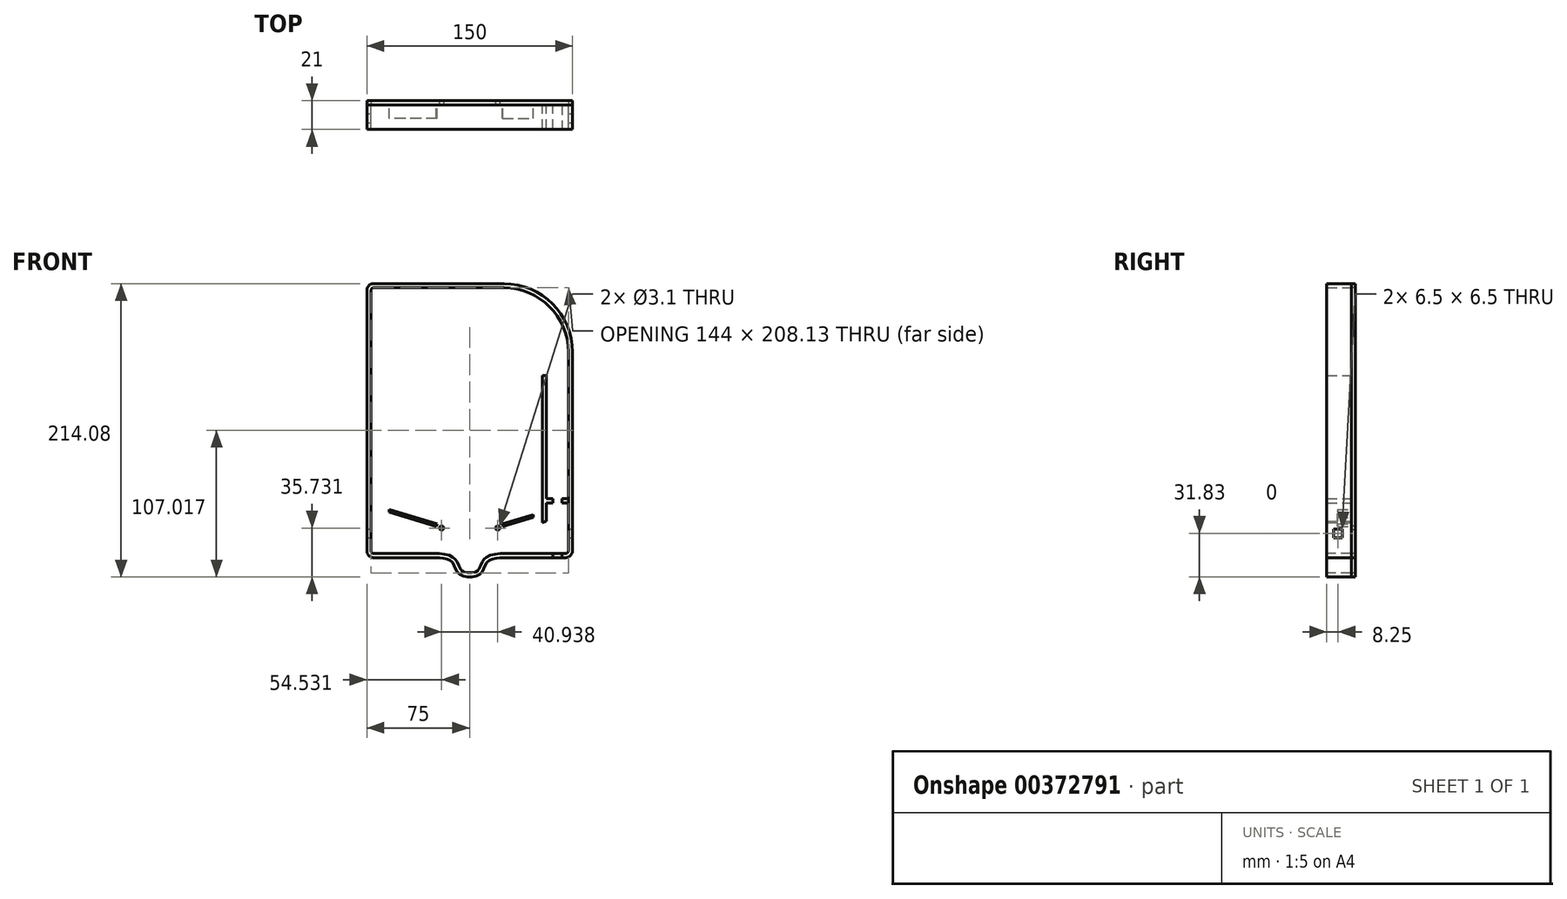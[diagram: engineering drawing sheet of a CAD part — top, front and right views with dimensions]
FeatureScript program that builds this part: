
annotation { "Feature Type Name" : "Feature", "Feature Type Description" : "" }
export const myFeature = defineFeature(function(context is Context, id is Id, definition is map)
    precondition{}
    {
        {
            var Q0;
            Q0=qCreatedBy(makeId("Front.planeOp"),FACE);
            var sketch = newSketch(context, id + "F0", { "sketchPlane" : qUnion([Q0])});
            skLineSegment(sketch, "E0.bottom", {"start": v(-70, 100) * mm, "end": v(25, 100) * mm});
            skLineSegment(sketch, "E0.top", {"start": v(-70, -100) * mm, "end": v(-25, -100) * mm});
            skLineSegment(sketch, "E0.left", {"start": v(-75, 95) * mm, "end": v(-75, -95) * mm});
            skLineSegment(sketch, "E0.right", {"start": v(75, 50) * mm, "end": v(75, -95) * mm});
            skPoint(sketch, "E1.visualSharp", {"position": v(75, 100) * mm});
            skArc(sketch, "E1.filletArc", {"start": v(75, 50) * mm, "mid": v(60.36, 85.36) * mm, "end": v(25, 100) * mm});
            skFitSpline(sketch, "E2", {"points": [v(-25, -100) * mm, v(-13, -103) * mm, v(-7.5, -112) * mm, v(7.5, -112) * mm, v(13, -103) * mm, v(25, -100) * mm], "startDerivative": vector(64.4, 0) * mm, "endDerivative": vector(59.8, 0) * mm});
            skLineSegment(sketch, "E3.trimOffspring", {"start": v(25, -100) * mm, "end": v(70, -100) * mm});
            skPoint(sketch, "E4.visualSharp", {"position": v(-75, -100) * mm});
            skArc(sketch, "E4.filletArc", {"start": v(-75, -95) * mm, "mid": v(-73.54, -98.54) * mm, "end": v(-70, -100) * mm});
            skPoint(sketch, "E5.visualSharp", {"position": v(75, -100) * mm});
            skArc(sketch, "E5.filletArc", {"start": v(70, -100) * mm, "mid": v(73.54, -98.54) * mm, "end": v(75, -95) * mm});
            skPoint(sketch, "E6.visualSharp", {"position": v(-75, 100) * mm});
            skArc(sketch, "E6.filletArc", {"start": v(-70, 100) * mm, "mid": v(-73.54, 98.54) * mm, "end": v(-75, 95) * mm});
            skArc(sketch, "E7.0", {"start": v(72, 50) * mm, "mid": v(58.23, 83.23) * mm, "end": v(25, 97) * mm});
            skLineSegment(sketch, "E7.1", {"start": v(-70, 97) * mm, "end": v(25, 97) * mm});
            skLineSegment(sketch, "E7.2", {"start": v(25, -97) * mm, "end": v(70, -97) * mm});
            skFitSpline(sketch, "E7.3", {"points": [v(-25, -97) * mm, v(-24.3, -97) * mm, v(-22.85, -97.02) * mm, v(-20.58, -97.16) * mm, v(-18.27, -97.45) * mm, v(-15.99, -97.96) * mm, v(-14.14, -98.64) * mm, v(-12.72, -99.4) * mm, v(-11.88, -99.98) * mm, v(-11.24, -100.52) * mm, v(-10.79, -100.96) * mm, v(-10.37, -101.43) * mm, v(-9.87, -102.07) * mm, v(-9.35, -102.88) * mm, v(-8.68, -104.15) * mm, v(-8.04, -105.65) * mm, v(-7.4, -107.23) * mm, v(-6.85, -108.28) * mm, v(-6.39, -108.93) * mm, v(-6.09, -109.26) * mm, v(-5.83, -109.5) * mm, v(-5.63, -109.66) * mm, v(-5.4, -109.82) * mm, v(-5.03, -110.03) * mm, v(-4.5, -110.3) * mm, v(-3.74, -110.57) * mm, v(-2.88, -110.79) * mm, v(-1.65, -111.01) * mm, v(0.01, -111.13) * mm, v(1.67, -111.01) * mm, v(2.9, -110.8) * mm, v(3.75, -110.57) * mm, v(4.5, -110.3) * mm, v(5.04, -110.04) * mm, v(5.4, -109.82) * mm, v(5.62, -109.66) * mm, v(5.82, -109.5) * mm, v(6.07, -109.27) * mm, v(6.36, -108.94) * mm, v(6.81, -108.3) * mm, v(7.35, -107.25) * mm, v(8, -105.66) * mm, v(8.65, -104.14) * mm, v(9.34, -102.85) * mm, v(9.88, -102.04) * mm, v(10.39, -101.4) * mm, v(10.82, -100.93) * mm, v(11.29, -100.48) * mm, v(11.94, -99.95) * mm, v(12.8, -99.37) * mm, v(14.25, -98.62) * mm, v(16.12, -97.95) * mm, v(18.43, -97.45) * mm, v(20.73, -97.16) * mm, v(22.96, -97.02) * mm, v(24.35, -97) * mm, v(25, -97) * mm]});
            skLineSegment(sketch, "E7.4", {"start": v(-70, -97) * mm, "end": v(-25, -97) * mm});
            skLineSegment(sketch, "E7.5", {"start": v(72, 50) * mm, "end": v(72, -95) * mm});
            skLineSegment(sketch, "E7.6", {"start": v(-72, 95) * mm, "end": v(-72, -95) * mm});
            skPoint(sketch, "E8.visualSharp", {"position": v(-72, -97) * mm});
            skArc(sketch, "E8.filletArc", {"start": v(-72, -95) * mm, "mid": v(-71.41, -96.41) * mm, "end": v(-70, -97) * mm});
            skPoint(sketch, "E9.visualSharp", {"position": v(72, -97) * mm});
            skArc(sketch, "E9.filletArc", {"start": v(70, -97) * mm, "mid": v(71.41, -96.41) * mm, "end": v(72, -95) * mm});
            skPoint(sketch, "E10.visualSharp", {"position": v(-72, 97) * mm});
            skArc(sketch, "E10.filletArc", {"start": v(-70, 97) * mm, "mid": v(-71.41, 96.41) * mm, "end": v(-72, 95) * mm});
            skSolve(sketch);
        }
        {
            var Q0;
            Q0=makeQuery(id+"F0.imprint","IMPRINT",FACE,{"disambiguationData":[TD([[makeQuery(id+"F0.imprint","IMPRINT",EDGE,{"derivedFrom":sQuery(id+"F0.wireOp",EDGE,"E0.bottom")}),-1.0]])]});
            extrude(context, id + "F1", {"entities" : qUnion([Q0]), "oppositeDirection" : true, "depth" : 3 * mm});
        }
        {
            var Q0;
            Q0=qCreatedBy(makeId("Front.planeOp"),FACE);
            var sketch = newSketch(context, id + "F2", { "sketchPlane" : qUnion([Q0])});
            skPoint(sketch, "E11.visualSharp", {"position": v(75, 100) * mm});
            skPoint(sketch, "E12.visualSharp", {"position": v(-75, -100) * mm});
            skPoint(sketch, "E13.visualSharp", {"position": v(75, -100) * mm});
            skPoint(sketch, "E14.visualSharp", {"position": v(-75, 100) * mm});
            skPoint(sketch, "E15.visualSharp", {"position": v(-72, -97) * mm});
            skPoint(sketch, "E16.visualSharp", {"position": v(72, -97.03) * mm});
            skPoint(sketch, "E17.visualSharp", {"position": v(-72, 97) * mm});
            skLineSegment(sketch, "E18", {"start": v(56, -76.55) * mm, "end": v(56, -60.03) * mm});
            skLineSegment(sketch, "E19.0", {"start": v(53, -74.41) * mm, "end": v(53, 32.97) * mm});
            skLineSegment(sketch, "E20", {"start": v(53, 32.97) * mm, "end": v(56, 32.97) * mm});
            skLineSegment(sketch, "E21", {"start": v(-23.73, -75.29) * mm, "end": v(-58.84, -64.8) * mm});
            skFitSpline(sketch, "E22", {"points": [v(-72, -68.6) * mm, v(-61.47, -71.7) * mm, v(-46.82, -77) * mm, v(-40.1, -82.63) * mm, v(-34.33, -91.08) * mm, v(-29.33, -95.27) * mm, v(-24.5, -97) * mm], "startDerivative": vector(53.73, -15.66) * mm, "endDerivative": vector(39.47, -11.28) * mm});
            skFitSpline(sketch, "E23.MirrorCS", {"points": [v(72, -68.6) * mm, v(61.47, -71.7) * mm, v(46.82, -77) * mm, v(40.1, -82.63) * mm, v(34.33, -91.08) * mm, v(29.33, -95.27) * mm, v(24.5, -97) * mm], "startDerivative": vector(-53.73, -15.66) * mm, "endDerivative": vector(-39.47, -11.28) * mm});
            skLineSegment(sketch, "E24.MirrorCS", {"start": v(23.73, -75.29) * mm, "end": v(46.34, -68.53) * mm});
            skFitSpline(sketch, "E25.0", {"points": [v(-72.84, -71.48) * mm, v(-71.72, -71.8) * mm, v(-69.48, -72.45) * mm, v(-66.54, -73.32) * mm, v(-64, -74.08) * mm, v(-61.97, -74.68) * mm, v(-59.82, -75.33) * mm, v(-56.88, -76.25) * mm, v(-53.94, -77.24) * mm, v(-51.23, -78.28) * mm, v(-49.68, -78.94) * mm, v(-48.56, -79.48) * mm, v(-47.54, -80) * mm, v(-46.42, -80.67) * mm, v(-45.28, -81.49) * mm, v(-44.28, -82.36) * mm, v(-43.34, -83.35) * mm, v(-42.43, -84.48) * mm, v(-41.48, -85.83) * mm, v(-40.5, -87.34) * mm, v(-39.48, -88.94) * mm, v(-38.43, -90.56) * mm, v(-37.5, -91.88) * mm, v(-36.72, -92.9) * mm, v(-35.9, -93.88) * mm, v(-34.85, -94.99) * mm, v(-33.53, -96.14) * mm, v(-32.38, -96.96) * mm, v(-31.45, -97.53) * mm, v(-30.74, -97.92) * mm, v(-30.02, -98.27) * mm, v(-29.08, -98.68) * mm, v(-27.92, -99.1) * mm, v(-26.58, -99.52) * mm, v(-25.74, -99.77) * mm, v(-25.33, -99.88) * mm]});
            skLineSegment(sketch, "E26.0", {"start": v(-24.3, -77.2) * mm, "end": v(-58.84, -66.88) * mm});
            skLineSegment(sketch, "E27.MirrorCS", {"start": v(24.3, -77.2) * mm, "end": v(46.34, -70.62) * mm});
            skLineSegment(sketch, "E28", {"start": v(-23.73, -75.29) * mm, "end": v(-24.3, -77.2) * mm});
            skLineSegment(sketch, "E29", {"start": v(23.73, -75.29) * mm, "end": v(24.3, -77.2) * mm});
            skLineSegment(sketch, "E30", {"start": v(46.34, -68.53) * mm, "end": v(46.34, -70.62) * mm});
            skLineSegment(sketch, "E31", {"start": v(-58.84, -64.8) * mm, "end": v(-58.84, -66.88) * mm});
            skPoint(sketch, "E32.orphan", {"position": v(-59.41, -66.71) * mm});
            skPoint(sketch, "E33.trimOffspring.end.orphan", {"position": v(58.84, -64.8) * mm});
            skPoint(sketch, "E34.trimOffspring.end.orphan", {"position": v(59.41, -66.71) * mm});
            skFitSpline(sketch, "E35.trimOffspring", {"points": [v(72.84, -71.48) * mm, v(71.72, -71.8) * mm, v(69.48, -72.45) * mm, v(66.54, -73.32) * mm, v(64, -74.08) * mm, v(61.97, -74.68) * mm, v(59.82, -75.33) * mm, v(56.88, -76.25) * mm, v(53.94, -77.24) * mm, v(51.23, -78.28) * mm, v(49.68, -78.94) * mm, v(48.56, -79.48) * mm, v(47.54, -80) * mm, v(46.42, -80.67) * mm, v(45.28, -81.49) * mm, v(44.28, -82.36) * mm, v(43.34, -83.35) * mm, v(42.43, -84.48) * mm, v(41.48, -85.83) * mm, v(40.5, -87.34) * mm, v(39.48, -88.94) * mm, v(38.43, -90.56) * mm, v(37.5, -91.88) * mm, v(36.72, -92.9) * mm, v(35.9, -93.88) * mm, v(34.85, -94.99) * mm, v(33.53, -96.14) * mm, v(32.38, -96.96) * mm, v(31.45, -97.53) * mm, v(30.74, -97.92) * mm, v(30.02, -98.27) * mm, v(29.08, -98.68) * mm, v(27.92, -99.1) * mm, v(26.58, -99.52) * mm, v(25.74, -99.77) * mm, v(25.33, -99.88) * mm]});
            skLineSegment(sketch, "E36", {"start": v(56, -57.03) * mm, "end": v(72, -57.03) * mm});
            skLineSegment(sketch, "E37.0", {"start": v(56, -60.03) * mm, "end": v(72, -60.03) * mm});
            skLineSegment(sketch, "E38.trimOffspring", {"start": v(56, -57.03) * mm, "end": v(56, 32.97) * mm});
            skLineSegment(sketch, "E39", {"start": v(-72, -68.6) * mm, "end": v(-72, -71.72) * mm});
            skLineSegment(sketch, "E40", {"start": v(-32.3, -97) * mm, "end": v(-24.5, -97) * mm});
            skLineSegment(sketch, "E41", {"start": v(24.5, -97) * mm, "end": v(32.24, -97.03) * mm});
            skLineSegment(sketch, "E42", {"start": v(72, -57.03) * mm, "end": v(72, -60.03) * mm});
            skSolve(sketch);
        }
        {
            var Q0;
            Q0=makeQuery(id+"F0.imprint","IMPRINT",FACE,{"disambiguationData":[TD([[makeQuery(id+"F0.imprint","IMPRINT",EDGE,{"derivedFrom":sQuery(id+"F0.wireOp",EDGE,"E0.bottom")}),-1.0]])]});
            extrude(context, id + "F3", {"entities" : qUnion([Q0]), "depth" : 18 * mm});
        }
        {
            var Q0;
            Q0=makeQuery(id+"F2.imprint","IMPRINT",FACE,{"disambiguationData":[TD([[makeQuery(id+"F2.imprint","IMPRINT",EDGE,{"derivedFrom":sQuery(id+"F2.wireOp",EDGE,"E24.MirrorCS")}),-1.0]])]});
            var Q1;
            Q1=makeQuery(id+"F2.imprint","IMPRINT",FACE,{"disambiguationData":[TD([[makeQuery(id+"F2.imprint","IMPRINT",EDGE,{"derivedFrom":sQuery(id+"F2.wireOp",EDGE,"E21")}),1.0]])]});
            extrude(context, id + "F4", {"entities" : qUnion([Q0, Q1]), "depth" : 10 * mm});
        }
        {
            var Q0;
            Q0=makeQuery(id+"F2.imprint","IMPRINT",FACE,{"disambiguationData":[TD([[makeQuery(id+"F2.imprint","IMPRINT",EDGE,{"derivedFrom":sQuery(id+"F2.wireOp",EDGE,"E22")}),-1.0]])]});
            var Q1;
            Q1=makeQuery(id+"F2.imprint","IMPRINT",FACE,{"disambiguationData":[TD([[makeQuery(id+"F2.imprint","IMPRINT",EDGE,{"derivedFrom":sQuery(id+"F2.wireOp",EDGE,"E18")}),1.0]])]});
            extrude(context, id + "F5", {"entities" : qUnion([Q0, Q1]), "depth" : 18 * mm});
        }
        {
            var Q0;
            Q0=qCreatedBy(makeId("Front.planeOp"),FACE);
            var sketch = newSketch(context, id + "F6", { "sketchPlane" : qUnion([Q0])});
            skLineSegment(sketch, "E43.bottom", {"start": v(-70, 100) * mm, "end": v(25, 100) * mm});
            skLineSegment(sketch, "E43.top", {"start": v(-70, -100) * mm, "end": v(-25, -100) * mm});
            skLineSegment(sketch, "E43.left", {"start": v(-75, 95) * mm, "end": v(-75, -95) * mm});
            skLineSegment(sketch, "E43.right", {"start": v(75, 50) * mm, "end": v(75, -95) * mm});
            skPoint(sketch, "E44.visualSharp", {"position": v(75, 100) * mm});
            skArc(sketch, "E44.filletArc", {"start": v(75, 50) * mm, "mid": v(60.36, 85.36) * mm, "end": v(25, 100) * mm});
            skFitSpline(sketch, "E45", {"points": [v(-25, -100) * mm, v(-13, -103) * mm, v(-7.5, -112) * mm, v(7.5, -112) * mm, v(13, -103) * mm, v(25, -100) * mm], "startDerivative": vector(64.4, 0) * mm, "endDerivative": vector(59.8, 0) * mm});
            skLineSegment(sketch, "E46.trimOffspring", {"start": v(25, -100) * mm, "end": v(70, -100) * mm});
            skPoint(sketch, "E47.visualSharp", {"position": v(-75, -100) * mm});
            skArc(sketch, "E47.filletArc", {"start": v(-75, -95) * mm, "mid": v(-73.54, -98.54) * mm, "end": v(-70, -100) * mm});
            skPoint(sketch, "E48.visualSharp", {"position": v(75, -100) * mm});
            skArc(sketch, "E48.filletArc", {"start": v(70, -100) * mm, "mid": v(73.54, -98.54) * mm, "end": v(75, -95) * mm});
            skPoint(sketch, "E49.visualSharp", {"position": v(-75, 100) * mm});
            skArc(sketch, "E49.filletArc", {"start": v(-70, 100) * mm, "mid": v(-73.54, 98.54) * mm, "end": v(-75, 95) * mm});
            skPoint(sketch, "E50.visualSharp", {"position": v(-66.45, -75.49) * mm});
            skPoint(sketch, "E51.visualSharp", {"position": v(77.55, -75.49) * mm});
            skPoint(sketch, "E52.visualSharp", {"position": v(-66.45, 118.51) * mm});
            skSolve(sketch);
        }
        {
            var Q0;
            Q0 = qSketchRegion(id + "F6", true);
            extrude(context, id + "F7", {"entities" : qUnion([Q0]), "oppositeDirection" : true, "depth" : 3 * mm});
        }
        {
            var Q0;
            Q0=makeQuery(id+"F3.opExtrude","SWEPT_FACE",FACE,{"disambiguationData":[OSD([sQuery(id+"F0.wireOp",EDGE,"E0.right")])]});
            var sketch = newSketch(context, id + "F8", { "sketchPlane" : qUnion([Q0])});
            skLineSegment(sketch, "E53.bottom", {"start": v(-13, -85.5) * mm, "end": v(-6.5, -85.5) * mm});
            skLineSegment(sketch, "E53.top", {"start": v(-13, -79) * mm, "end": v(-6.5, -79) * mm});
            skLineSegment(sketch, "E53.left", {"start": v(-13, -85.5) * mm, "end": v(-13, -79) * mm});
            skLineSegment(sketch, "E53.right", {"start": v(-6.5, -85.5) * mm, "end": v(-6.5, -79) * mm});
            skSolve(sketch);
        }
        {
            var Q0;
            Q0=makeQuery(id+"F8.imprint","IMPRINT",FACE,{"disambiguationData":[TD([[makeQuery(id+"F8.imprint","IMPRINT",EDGE,{"derivedFrom":sQuery(id+"F8.wireOp",EDGE,"E53.bottom")}),1.0]])]});
            extrude(context, id + "F9", {"entities" : qUnion([Q0]), "operationType" : NewBodyOperationType.REMOVE, "endBound" : BoundingType.THROUGH_ALL, "oppositeDirection" : true, "depth" : 25 * mm});
        }
        {
            var Q0;
            Q0=makeQuery(id+"F8.imprint","IMPRINT",FACE,{"disambiguationData":[TD([[makeQuery(id+"F8.imprint","IMPRINT",EDGE,{"derivedFrom":sQuery(id+"F8.wireOp",EDGE,"E53.bottom")}),1.0]])]});
            extrude(context, id + "F10", {"entities" : qUnion([Q0]), "operationType" : NewBodyOperationType.REMOVE, "endBound" : BoundingType.THROUGH_ALL, "oppositeDirection" : true, "depth" : 25 * mm});
        }
        {
            var Q0;
            Q0=makeQuery(id+"F3.opExtrude","SWEPT_FACE",FACE,{"disambiguationData":[OSD([sQuery(id+"F0.wireOp",EDGE,"E3.trimOffspring")])]});
            var sketch = newSketch(context, id + "F11", { "sketchPlane" : qUnion([Q0])});
            skLineSegment(sketch, "E54.bottom", {"start": v(60.75, 21.91) * mm, "end": v(67.25, 21.91) * mm});
            skLineSegment(sketch, "E54.top", {"start": v(60.75, 0) * mm, "end": v(67.25, 0) * mm});
            skLineSegment(sketch, "E54.left", {"start": v(60.75, 21.91) * mm, "end": v(60.75, 0) * mm});
            skLineSegment(sketch, "E54.right", {"start": v(67.25, 21.91) * mm, "end": v(67.25, 0) * mm});
            skPoint(sketch, "E55.startSnap0", {"position": v(64, 21.91) * mm});
            skSolve(sketch);
        }
        {
            var Q0;
            {var subQ0=sQuery(id+"F11.wireOp",EDGE,"E54.top");Q0=makeQuery(id+"F11.imprint","IMPRINT",FACE,{"disambiguationData":[TD([[makeQuery(id+"F11.imprint","IMPRINT",EDGE,{"derivedFrom":subQ0}),1.0]])]});}
            var Q1;
            Q1=makeQuery(id+"F5.opExtrude","SWEPT_FACE",FACE,{"disambiguationData":[OSD([sQuery(id+"F2.wireOp",EDGE,"E36")])]});
            extrude(context, id + "F12", {"entities" : qUnion([Q0]), "operationType" : NewBodyOperationType.REMOVE, "endBound" : BoundingType.UP_TO_SURFACE, "oppositeDirection" : true, "endBoundEntityFace" : qUnion([Q1]), "depth" : 25 * mm});
        }
        {
            var Q0;
            Q0=makeQuery(id+"F7.opExtrude","CAP_FACE",FACE,{"disambiguationData":[OSD([sQuery(id+"F6.wireOp",EDGE,"E43.bottom"),sQuery(id+"F6.wireOp",EDGE,"E43.top"),sQuery(id+"F6.wireOp",EDGE,"E43.left"),sQuery(id+"F6.wireOp",EDGE,"E43.right"),sQuery(id+"F6.wireOp",EDGE,"E44.filletArc"),sQuery(id+"F6.wireOp",EDGE,"E45"),sQuery(id+"F6.wireOp",EDGE,"E46.trimOffspring"),sQuery(id+"F6.wireOp",EDGE,"E47.filletArc"),sQuery(id+"F6.wireOp",EDGE,"E48.filletArc"),sQuery(id+"F6.wireOp",EDGE,"E49.filletArc")])],"isStart":true});
            var sketch = newSketch(context, id + "F13", { "sketchPlane" : qUnion([Q0])});
            skCircle(sketch, "E56", {"center": v(-20.47, -78.35) * mm, "radius": 1.55 * mm});
            skCircle(sketch, "E57", {"center": v(20.47, -78.35) * mm, "radius": 1.55 * mm});
            skSolve(sketch);
        }
        {
            var Q0;
            Q0 = qSketchRegion(id + "F13", true);
            extrude(context, id + "F14", {"entities" : qUnion([Q0]), "operationType" : NewBodyOperationType.REMOVE, "endBound" : BoundingType.THROUGH_ALL, "oppositeDirection" : true, "depth" : 25 * mm});
        }
    });
